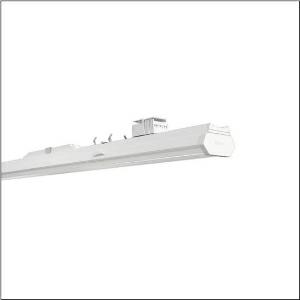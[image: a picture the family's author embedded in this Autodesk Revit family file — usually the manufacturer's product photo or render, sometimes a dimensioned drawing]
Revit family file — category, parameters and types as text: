
# Revit family: licross_r__11_protected_extreme_ho_51td1bdn4e5me_a1af
name_source: partatom
category: Lighting Fixtures
units: mm (PartAtom-declared; Revit-internal decimal feet)

## family parameters
Cut with Voids When Loaded = No
Host = Face
Light Source = No
Part Type = Normal
Room Calculation Point = No
Round Connector Dimension = Use Diameter
Shared = No

## types (1)
- --- (1 x LED, 14500 lm, 87.3 W, 4000K)
    Apparent Load = 87 VA
    CIE Flux Codes = 54 82 95 97 100
    Color Rendering = 80
    Color Temperature = 4000K
    Default Elevation = 1800 mm
    Description = Licross® 11 Protected extreme HO, luminaire insert, of sheet steel, galvanised, coil coated, white, length: 1.500mm, width: 90mm, height: 101mm, LED rated luminous flux: 14.500lm, light colour: 840, control gear: DALI 2, with plug, 5-pole, with phase selection, mains connection: 220..240V, AC, 50/60Hz, rated input power: 87W, halogen-free wiring, primary optical cover: cover, of PMMA, light emission: direct distribution, primary light characteristic: symmetric, protection rating (complete): IP54, insulation class (complete): insulation class I (protective earthing), certification: CE, ENEC, VDE, UKCA, protection symbol: D if used in an environment with non-conductive dust loads with corresponding accessories, impact resistance: IK06, permissible ambient temperature for indoor applications: -40..+40°C, corresponds to IFS (International Featured Standards) requirements for safety and quality in the food industry, reducing of maximum allowable ambient temperature of 5°C with ceiling mounting, LABS conformity tested according to VDMA 24364:2018-05, packaging unit: 1 piece
    Height = 92 mm
    Lamp = 1 x LED
    Lamp Light Flux = 14500 lm
    Lamp Power = 87.3 W
    Lamp count = 1
    Length = 1500 mm
    Luminous efficacy = 166 lm/W
    Manufacturer = Siteco
    ModVariant = No
    Model = 51TD1BDN4E5ME
    Mounting Place = Ceiling
    Mounting Type = Pendant
    Number of Poles = 1
    OnlyDefault = Yes
    Power Factor = 1
    Product Name = Licross® 11 Protected extreme HO
    Product group = luminaire insert
    ProductGroupID = 902
    Protection Class = Protection class I
    Protection Degree = IP 54
    RLX_Detail_Level = 1
    RLX_Emergency_Light_Flux = 0 lm
    RLX_Emergency_Type = 0
    RLX_Emergency_Type_DB = No
    RlxData = <blob elided: 24269 chars, md5=2f905a7e>
    Socket = socket
    Standby Power = 0 W
    System Light Flux = 14500 lm
    System Power = 87 W
    Type Comments = factory setting: luminous flux: 100 % | dim-lin: 254 | 589 mA
    Type Image = l_1256145.jpg
    URL = http://relux.com
    VarID = @adj_082906
    Voltage = 0 V
    Weight = 0.00 kg
    Width = 88 mm

## geometry (parser evidence)
native form markers: Blend x4, Sweep x9
no freeform markers — native parametric forms only
